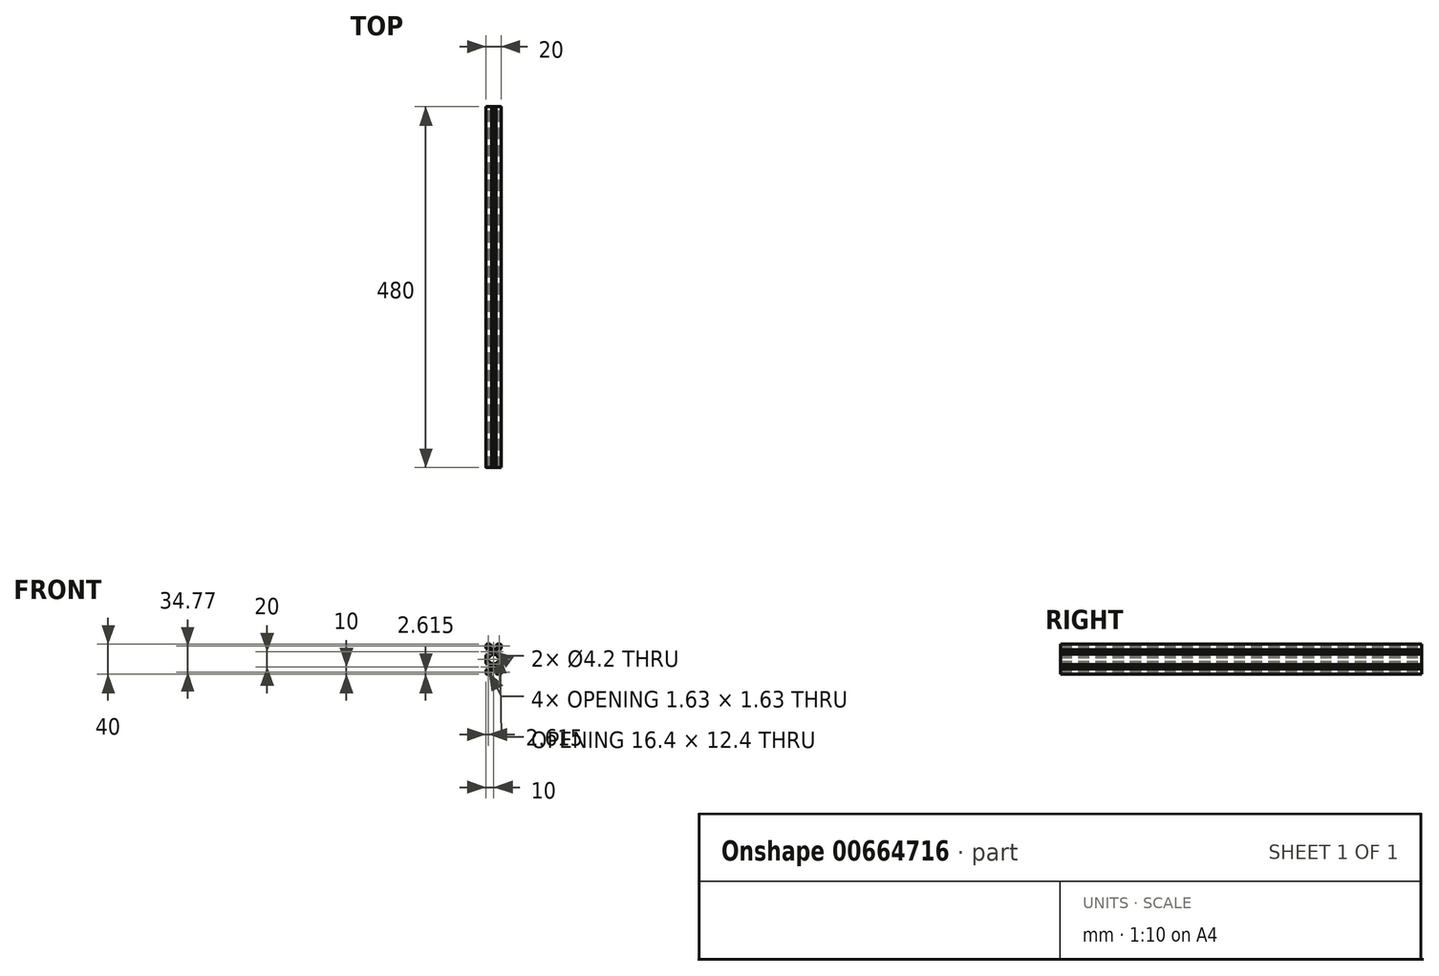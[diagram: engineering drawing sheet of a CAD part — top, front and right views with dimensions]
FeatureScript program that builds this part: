
annotation { "Feature Type Name" : "Feature", "Feature Type Description" : "" }
export const myFeature = defineFeature(function(context is Context, id is Id, definition is map)
    precondition{}
    {
        {
            var Q0;
            Q0=qCreatedBy(makeId("Front.planeOp"),FACE);
            var sketch = newSketch(context, id + "F0", { "sketchPlane" : qUnion([Q0])});
            skLineSegment(sketch, "E0", {"start": v(1.5, 0) * mm, "end": v(5.1, 0) * mm});
            skLineSegment(sketch, "E1", {"start": v(0, -1.5) * mm, "end": v(0, -5.1) * mm});
            skLineSegment(sketch, "E2", {"start": v(5.65, -0.23) * mm, "end": v(7.11, -1.69) * mm});
            skLineSegment(sketch, "E3", {"start": v(7.11, -1.7) * mm, "end": v(7.11, -1.8) * mm});
            skLineSegment(sketch, "E4", {"start": v(0.23, -5.65) * mm, "end": v(1.69, -7.11) * mm});
            skLineSegment(sketch, "E5", {"start": v(1.7, -7.11) * mm, "end": v(1.8, -7.11) * mm});
            skLineSegment(sketch, "E6", {"start": v(1.8, -7.11) * mm, "end": v(1.8, -4.5) * mm});
            skLineSegment(sketch, "E7", {"start": v(1.8, -4.5) * mm, "end": v(3.44, -4.5) * mm});
            skLineSegment(sketch, "E8", {"start": v(7.11, -1.8) * mm, "end": v(4.5, -1.8) * mm});
            skLineSegment(sketch, "E9", {"start": v(4.5, -1.8) * mm, "end": v(4.5, -3.44) * mm});
            skPoint(sketch, "E10.visualSharp", {"position": v(0, 0) * mm});
            skArc(sketch, "E10.filletArc", {"start": v(1.5, 0) * mm, "mid": v(0.44, -0.44) * mm, "end": v(0, -1.5) * mm});
            skPoint(sketch, "E11.visualSharp", {"position": v(5.42, 0) * mm});
            skArc(sketch, "E11.filletArc", {"start": v(5.65, -0.23) * mm, "mid": v(5.4, -0.06) * mm, "end": v(5.1, 0) * mm});
            skPoint(sketch, "E12.visualSharp", {"position": v(0, -5.42) * mm});
            skArc(sketch, "E12.filletArc", {"start": v(0, -5.1) * mm, "mid": v(0.06, -5.4) * mm, "end": v(0.23, -5.65) * mm});
            skLineSegment(sketch, "E13", {"start": v(1.8, -4.5) * mm, "end": v(1.8, 0) * mm, "construction": true});
            skLineSegment(sketch, "E14", {"start": v(4.5, -1.8) * mm, "end": v(0, -1.8) * mm, "construction": true});
            skPoint(sketch, "E15", {"position": v(1.8, -1.8) * mm});
            skLineSegment(sketch, "E16", {"start": v(1.8, -1.8) * mm, "end": v(3.43, -1.8) * mm});
            skLineSegment(sketch, "E17", {"start": v(3.43, -1.8) * mm, "end": v(3.43, -2.34) * mm});
            skLineSegment(sketch, "E18", {"start": v(1.8, -1.8) * mm, "end": v(1.8, -3.43) * mm});
            skLineSegment(sketch, "E19", {"start": v(1.8, -3.43) * mm, "end": v(2.34, -3.43) * mm});
            skLineSegment(sketch, "E20", {"start": v(2.34, -3.43) * mm, "end": v(3.43, -2.34) * mm});
            skArc(sketch, "E21", {"start": v(10, -7.9) * mm, "mid": v(8.52, -8.52) * mm, "end": v(7.9, -10) * mm});
            skLineSegment(sketch, "E22", {"start": v(10, -7.9) * mm, "end": v(10, -6.2) * mm, "construction": true});
            skLineSegment(sketch, "E23", {"start": v(9.9, -6.1) * mm, "end": v(7.16, -6.1) * mm});
            skLineSegment(sketch, "E24", {"start": v(7.16, -6.1) * mm, "end": v(4.5, -3.44) * mm});
            skLineSegment(sketch, "E25", {"start": v(7.9, -10) * mm, "end": v(6.2, -10) * mm, "construction": true});
            skLineSegment(sketch, "E26", {"start": v(6.1, -9.9) * mm, "end": v(6.1, -7.16) * mm});
            skLineSegment(sketch, "E27", {"start": v(6.1, -7.16) * mm, "end": v(3.44, -4.5) * mm});
            skLineSegment(sketch, "E28", {"start": v(1.8, -1.8) * mm, "end": v(10, -10) * mm, "construction": true});
            skLineSegment(sketch, "E29", {"start": v(6.2, -10) * mm, "end": v(6.1, -9.9) * mm});
            skLineSegment(sketch, "E30", {"start": v(10, -6.2) * mm, "end": v(9.9, -6.1) * mm});
            skArc(sketch, "E31", {"start": v(7.9, -10) * mm, "mid": v(8.52, -11.48) * mm, "end": v(10, -12.1) * mm});
            skLineSegment(sketch, "E32", {"start": v(6.2, -10) * mm, "end": v(6.1, -10.1) * mm});
            skLineSegment(sketch, "E33", {"start": v(6.1, -10.1) * mm, "end": v(6.1, -12.84) * mm});
            skLineSegment(sketch, "E34", {"start": v(10, -12.1) * mm, "end": v(10, -13.8) * mm, "construction": true});
            skLineSegment(sketch, "E35", {"start": v(10, -13.8) * mm, "end": v(9.9, -13.9) * mm});
            skLineSegment(sketch, "E36", {"start": v(9.9, -13.9) * mm, "end": v(7.16, -13.9) * mm});
            skLineSegment(sketch, "E37", {"start": v(6.1, -12.84) * mm, "end": v(7.16, -13.9) * mm, "construction": true});
            skLineSegment(sketch, "E38", {"start": v(7.16, -6.1) * mm, "end": v(6.1, -7.16) * mm, "construction": true});
            skLineSegment(sketch, "E39", {"start": v(6.1, -12.84) * mm, "end": v(3.44, -15.5) * mm});
            skLineSegment(sketch, "E40", {"start": v(7.16, -13.9) * mm, "end": v(3.76, -17.3) * mm});
            skLineSegment(sketch, "E41", {"start": v(10, -10) * mm, "end": v(1.8, -18.2) * mm, "construction": true});
            skLineSegment(sketch, "E42", {"start": v(3.44, -15.5) * mm, "end": v(1.8, -15.5) * mm});
            skLineSegment(sketch, "E43", {"start": v(1.8, -15.5) * mm, "end": v(1.8, -12.89) * mm});
            skLineSegment(sketch, "E44", {"start": v(1.8, -12.89) * mm, "end": v(1.7, -12.89) * mm});
            skLineSegment(sketch, "E45", {"start": v(1.7, -12.89) * mm, "end": v(0.23, -14.35) * mm});
            skLineSegment(sketch, "E46", {"start": v(0, -14.9) * mm, "end": v(0, -20) * mm});
            skLineSegment(sketch, "E47", {"start": v(0, -20) * mm, "end": v(1.8, -20) * mm, "construction": true});
            skLineSegment(sketch, "E48", {"start": v(1.8, -20) * mm, "end": v(1.8, -17.3) * mm});
            skLineSegment(sketch, "E49", {"start": v(1.8, -17.3) * mm, "end": v(3.76, -17.3) * mm});
            skPoint(sketch, "E50.visualSharp", {"position": v(0, -14.58) * mm});
            skArc(sketch, "E50.filletArc", {"start": v(0.23, -14.35) * mm, "mid": v(0.06, -14.6) * mm, "end": v(0, -14.9) * mm});
            skLineSegment(sketch, "E51.MirrorCS", {"start": v(13.8, -10) * mm, "end": v(13.9, -10.1) * mm});
            skLineSegment(sketch, "E52.MirrorCS", {"start": v(13.8, -10) * mm, "end": v(13.9, -9.9) * mm});
            skLineSegment(sketch, "E53.MirrorCS", {"start": v(12.9, -1.69) * mm, "end": v(12.9, -1.8) * mm});
            skLineSegment(sketch, "E54.MirrorCS", {"start": v(16.57, -1.8) * mm, "end": v(16.57, -2.34) * mm});
            skLineSegment(sketch, "E55.MirrorCS", {"start": v(10, -13.8) * mm, "end": v(10.1, -13.9) * mm});
            skLineSegment(sketch, "E56.MirrorCS", {"start": v(12.84, -6.1) * mm, "end": v(13.9, -7.16) * mm, "construction": true});
            skArc(sketch, "E57.MirrorCS", {"start": v(14.35, -0.23) * mm, "mid": v(14.6, -0.06) * mm, "end": v(14.9, 0) * mm});
            skArc(sketch, "E58.MirrorCS", {"start": v(20, -5.1) * mm, "mid": v(19.94, -5.4) * mm, "end": v(19.77, -5.65) * mm});
            skLineSegment(sketch, "E59.MirrorCS", {"start": v(13.9, -12.84) * mm, "end": v(12.84, -13.9) * mm, "construction": true});
            skArc(sketch, "E60.MirrorCS", {"start": v(19.77, -14.35) * mm, "mid": v(19.94, -14.6) * mm, "end": v(20, -14.9) * mm});
            skLineSegment(sketch, "E61.MirrorCS", {"start": v(18.31, -7.11) * mm, "end": v(18.2, -7.11) * mm});
            skLineSegment(sketch, "E62.MirrorCS", {"start": v(10, -6.2) * mm, "end": v(10.1, -6.1) * mm});
            skLineSegment(sketch, "E63.MirrorCS", {"start": v(18.2, -3.43) * mm, "end": v(17.66, -3.43) * mm});
            skLineSegment(sketch, "E64.MirrorCS", {"start": v(18.2, -12.89) * mm, "end": v(18.31, -12.89) * mm});
            skLineSegment(sketch, "E65.MirrorCS", {"start": v(17.66, -3.43) * mm, "end": v(16.57, -2.34) * mm});
            skLineSegment(sketch, "E66.MirrorCS", {"start": v(18.31, -12.89) * mm, "end": v(19.77, -14.35) * mm});
            skLineSegment(sketch, "E67.MirrorCS", {"start": v(18.2, -1.8) * mm, "end": v(16.57, -1.8) * mm});
            skArc(sketch, "E68.MirrorCS", {"start": v(18.5, 0) * mm, "mid": v(19.56, -0.44) * mm, "end": v(20, -1.5) * mm});
            skLineSegment(sketch, "E69.MirrorCS", {"start": v(15.5, -1.8) * mm, "end": v(15.5, -3.44) * mm});
            skLineSegment(sketch, "E70.MirrorCS", {"start": v(12.1, -10) * mm, "end": v(13.8, -10) * mm, "construction": true});
            skLineSegment(sketch, "E71.MirrorCS", {"start": v(18.2, -1.8) * mm, "end": v(18.2, -3.43) * mm});
            skPoint(sketch, "E72.MirrorP", {"position": v(18.2, -1.8) * mm});
            skLineSegment(sketch, "E73.MirrorCS", {"start": v(10.1, -6.1) * mm, "end": v(12.84, -6.1) * mm});
            skLineSegment(sketch, "E74.MirrorCS", {"start": v(20, -20) * mm, "end": v(18.2, -20) * mm, "construction": true});
            skLineSegment(sketch, "E75.MirrorCS", {"start": v(18.2, -7.11) * mm, "end": v(18.2, -4.5) * mm});
            skLineSegment(sketch, "E76.MirrorCS", {"start": v(18.5, 0) * mm, "end": v(14.9, 0) * mm});
            skLineSegment(sketch, "E77.MirrorCS", {"start": v(12.84, -6.1) * mm, "end": v(15.5, -3.44) * mm});
            skArc(sketch, "E78.MirrorCS", {"start": v(12.1, -10) * mm, "mid": v(11.48, -11.48) * mm, "end": v(10, -12.1) * mm});
            skLineSegment(sketch, "E79.MirrorCS", {"start": v(12.84, -13.9) * mm, "end": v(16.24, -17.3) * mm});
            skLineSegment(sketch, "E80.MirrorCS", {"start": v(13.9, -7.16) * mm, "end": v(16.56, -4.5) * mm});
            skLineSegment(sketch, "E81.MirrorCS", {"start": v(20, -14.9) * mm, "end": v(20, -20) * mm});
            skLineSegment(sketch, "E82.MirrorCS", {"start": v(13.9, -12.84) * mm, "end": v(16.56, -15.5) * mm});
            skLineSegment(sketch, "E83.MirrorCS", {"start": v(18.2, -20) * mm, "end": v(18.2, -17.3) * mm});
            skLineSegment(sketch, "E84.MirrorCS", {"start": v(14.35, -0.23) * mm, "end": v(12.9, -1.69) * mm});
            skPoint(sketch, "E85.MirrorP", {"position": v(20, 0) * mm});
            skLineSegment(sketch, "E86.MirrorCS", {"start": v(18.2, -4.5) * mm, "end": v(16.56, -4.5) * mm});
            skLineSegment(sketch, "E87.MirrorCS", {"start": v(12.9, -1.8) * mm, "end": v(15.5, -1.8) * mm});
            skPoint(sketch, "E88.MirrorP", {"position": v(20, -14.58) * mm});
            skLineSegment(sketch, "E89.MirrorCS", {"start": v(20, -1.5) * mm, "end": v(20, -5.1) * mm});
            skLineSegment(sketch, "E90.MirrorCS", {"start": v(18.2, -15.5) * mm, "end": v(18.2, -12.89) * mm});
            skLineSegment(sketch, "E91.MirrorCS", {"start": v(16.56, -15.5) * mm, "end": v(18.2, -15.5) * mm});
            skLineSegment(sketch, "E92.MirrorCS", {"start": v(13.9, -9.9) * mm, "end": v(13.9, -7.16) * mm});
            skArc(sketch, "E93.MirrorCS", {"start": v(10, -7.9) * mm, "mid": v(11.48, -8.52) * mm, "end": v(12.1, -10) * mm});
            skPoint(sketch, "E94.MirrorP", {"position": v(14.58, 0) * mm});
            skLineSegment(sketch, "E95.MirrorCS", {"start": v(18.2, -4.5) * mm, "end": v(18.2, 0) * mm, "construction": true});
            skLineSegment(sketch, "E96.MirrorCS", {"start": v(15.5, -1.8) * mm, "end": v(20, -1.8) * mm, "construction": true});
            skLineSegment(sketch, "E97.MirrorCS", {"start": v(10, -10) * mm, "end": v(18.2, -18.2) * mm, "construction": true});
            skLineSegment(sketch, "E98.MirrorCS", {"start": v(18.2, -17.3) * mm, "end": v(16.24, -17.3) * mm});
            skLineSegment(sketch, "E99.MirrorCS", {"start": v(18.2, -1.8) * mm, "end": v(10, -10) * mm, "construction": true});
            skLineSegment(sketch, "E100.MirrorCS", {"start": v(10.1, -13.9) * mm, "end": v(12.84, -13.9) * mm});
            skPoint(sketch, "E101.MirrorP", {"position": v(20, -5.42) * mm});
            skLineSegment(sketch, "E102.MirrorCS", {"start": v(19.77, -5.65) * mm, "end": v(18.31, -7.11) * mm});
            skLineSegment(sketch, "E103.MirrorCS", {"start": v(13.9, -10.1) * mm, "end": v(13.9, -12.84) * mm});
            skLineSegment(sketch, "E104.MirrorCS", {"start": v(6.2, -30) * mm, "end": v(6.1, -29.9) * mm});
            skLineSegment(sketch, "E105.MirrorCS", {"start": v(6.2, -30) * mm, "end": v(6.1, -30.1) * mm});
            skLineSegment(sketch, "E106.MirrorCS", {"start": v(13.8, -30) * mm, "end": v(13.9, -30.1) * mm});
            skLineSegment(sketch, "E107.MirrorCS", {"start": v(13.8, -30) * mm, "end": v(13.9, -29.9) * mm});
            skLineSegment(sketch, "E108.MirrorCS", {"start": v(10, -26.2) * mm, "end": v(9.9, -26.1) * mm});
            skLineSegment(sketch, "E109.MirrorCS", {"start": v(10, -26.2) * mm, "end": v(10.1, -26.1) * mm});
            skArc(sketch, "E110.MirrorCS", {"start": v(14.35, -39.77) * mm, "mid": v(14.6, -39.94) * mm, "end": v(14.9, -40) * mm});
            skLineSegment(sketch, "E111.MirrorCS", {"start": v(10, -33.8) * mm, "end": v(9.9, -33.9) * mm});
            skArc(sketch, "E112.MirrorCS", {"start": v(0.23, -25.65) * mm, "mid": v(0.06, -25.4) * mm, "end": v(0, -25.1) * mm});
            skArc(sketch, "E113.MirrorCS", {"start": v(19.77, -25.65) * mm, "mid": v(19.94, -25.4) * mm, "end": v(20, -25.1) * mm});
            skArc(sketch, "E114.MirrorCS", {"start": v(5.65, -39.77) * mm, "mid": v(5.4, -39.94) * mm, "end": v(5.1, -40) * mm});
            skLineSegment(sketch, "E115.MirrorCS", {"start": v(10, -33.8) * mm, "end": v(10.1, -33.9) * mm});
            skLineSegment(sketch, "E116.MirrorCS", {"start": v(7.11, -38.3) * mm, "end": v(7.11, -38.2) * mm});
            skLineSegment(sketch, "E117.MirrorCS", {"start": v(18.2, -36.57) * mm, "end": v(17.66, -36.57) * mm});
            skArc(sketch, "E118.MirrorCS", {"start": v(0, -34.9) * mm, "mid": v(0.06, -34.6) * mm, "end": v(0.23, -34.35) * mm});
            skLineSegment(sketch, "E119.MirrorCS", {"start": v(1.8, -36.57) * mm, "end": v(2.34, -36.57) * mm});
            skLineSegment(sketch, "E120.MirrorCS", {"start": v(3.43, -38.2) * mm, "end": v(3.43, -37.66) * mm});
            skLineSegment(sketch, "E121.MirrorCS", {"start": v(1.8, -27.11) * mm, "end": v(1.7, -27.11) * mm});
            skLineSegment(sketch, "E122.MirrorCS", {"start": v(18.31, -32.89) * mm, "end": v(18.2, -32.89) * mm});
            skLineSegment(sketch, "E123.MirrorCS", {"start": v(12.9, -38.31) * mm, "end": v(12.9, -38.2) * mm});
            skLineSegment(sketch, "E124.MirrorCS", {"start": v(16.57, -38.2) * mm, "end": v(16.57, -37.66) * mm});
            skLineSegment(sketch, "E125.MirrorCS", {"start": v(10, -27.9) * mm, "end": v(10, -26.2) * mm, "construction": true});
            skLineSegment(sketch, "E126.MirrorCS", {"start": v(1.7, -32.9) * mm, "end": v(1.8, -32.9) * mm});
            skLineSegment(sketch, "E127.MirrorCS", {"start": v(18.2, -27.11) * mm, "end": v(18.31, -27.11) * mm});
            skArc(sketch, "E128.MirrorCS", {"start": v(20, -34.9) * mm, "mid": v(19.94, -34.6) * mm, "end": v(19.77, -34.35) * mm});
            skLineSegment(sketch, "E129.MirrorCS", {"start": v(2.34, -36.57) * mm, "end": v(3.43, -37.66) * mm});
            skLineSegment(sketch, "E130.MirrorCS", {"start": v(13.9, -27.16) * mm, "end": v(12.84, -26.1) * mm, "construction": true});
            skLineSegment(sketch, "E131.MirrorCS", {"start": v(1.8, -38.2) * mm, "end": v(3.43, -38.2) * mm});
            skLineSegment(sketch, "E132.MirrorCS", {"start": v(1.69, -27.11) * mm, "end": v(0.23, -25.65) * mm});
            skLineSegment(sketch, "E133.MirrorCS", {"start": v(17.66, -36.57) * mm, "end": v(16.57, -37.66) * mm});
            skLineSegment(sketch, "E134.MirrorCS", {"start": v(4.5, -38.2) * mm, "end": v(4.5, -36.56) * mm});
            skLineSegment(sketch, "E135.MirrorCS", {"start": v(6.1, -27.16) * mm, "end": v(7.16, -26.1) * mm, "construction": true});
            skLineSegment(sketch, "E136.MirrorCS", {"start": v(1.8, -38.2) * mm, "end": v(1.8, -36.57) * mm});
            skLineSegment(sketch, "E137.MirrorCS", {"start": v(18.2, -38.2) * mm, "end": v(18.2, -36.57) * mm});
            skLineSegment(sketch, "E138.MirrorCS", {"start": v(18.2, -38.2) * mm, "end": v(16.57, -38.2) * mm});
            skPoint(sketch, "E139.MirrorP", {"position": v(20, -40) * mm});
            skLineSegment(sketch, "E140.MirrorCS", {"start": v(18.2, -22.7) * mm, "end": v(16.24, -22.7) * mm});
            skLineSegment(sketch, "E141.MirrorCS", {"start": v(7.16, -26.1) * mm, "end": v(3.76, -22.7) * mm});
            skPoint(sketch, "E142.MirrorP", {"position": v(18.2, -38.2) * mm});
            skPoint(sketch, "E143.MirrorP", {"position": v(14.58, -40) * mm});
            skLineSegment(sketch, "E144.MirrorCS", {"start": v(6.1, -32.84) * mm, "end": v(3.44, -35.5) * mm});
            skArc(sketch, "E145.MirrorCS", {"start": v(18.5, -40) * mm, "mid": v(19.56, -39.56) * mm, "end": v(20, -38.5) * mm});
            skLineSegment(sketch, "E146.MirrorCS", {"start": v(16.56, -24.5) * mm, "end": v(18.2, -24.5) * mm});
            skLineSegment(sketch, "E147.MirrorCS", {"start": v(19.77, -34.35) * mm, "end": v(18.31, -32.89) * mm});
            skLineSegment(sketch, "E148.MirrorCS", {"start": v(18.5, -40) * mm, "end": v(14.9, -40) * mm});
            skArc(sketch, "E149.MirrorCS", {"start": v(12.1, -30) * mm, "mid": v(11.48, -28.52) * mm, "end": v(10, -27.9) * mm});
            skLineSegment(sketch, "E150.MirrorCS", {"start": v(7.16, -33.9) * mm, "end": v(4.5, -36.56) * mm});
            skLineSegment(sketch, "E151.MirrorCS", {"start": v(12.1, -30) * mm, "end": v(13.8, -30) * mm, "construction": true});
            skLineSegment(sketch, "E152.MirrorCS", {"start": v(1.8, -35.5) * mm, "end": v(1.8, -40) * mm, "construction": true});
            skLineSegment(sketch, "E153.MirrorCS", {"start": v(18.2, -38.2) * mm, "end": v(10, -30) * mm, "construction": true});
            skLineSegment(sketch, "E154.MirrorCS", {"start": v(4.5, -38.2) * mm, "end": v(0, -38.2) * mm, "construction": true});
            skLineSegment(sketch, "E155.MirrorCS", {"start": v(10, -30) * mm, "end": v(18.2, -21.8) * mm, "construction": true});
            skLineSegment(sketch, "E156.MirrorCS", {"start": v(15.5, -38.2) * mm, "end": v(15.5, -36.56) * mm});
            skLineSegment(sketch, "E157.MirrorCS", {"start": v(1.5, -40) * mm, "end": v(5.1, -40) * mm});
            skLineSegment(sketch, "E158.MirrorCS", {"start": v(10, -32.1) * mm, "end": v(10, -33.8) * mm, "construction": true});
            skPoint(sketch, "E159.MirrorP", {"position": v(1.8, -38.2) * mm});
            skLineSegment(sketch, "E160.MirrorCS", {"start": v(7.9, -30) * mm, "end": v(6.2, -30) * mm, "construction": true});
            skArc(sketch, "E161.MirrorCS", {"start": v(1.5, -40) * mm, "mid": v(0.44, -39.56) * mm, "end": v(0, -38.5) * mm});
            skLineSegment(sketch, "E162.MirrorCS", {"start": v(12.84, -26.1) * mm, "end": v(16.24, -22.7) * mm});
            skLineSegment(sketch, "E163.MirrorCS", {"start": v(12.9, -38.2) * mm, "end": v(15.5, -38.2) * mm});
            skLineSegment(sketch, "E164.MirrorCS", {"start": v(7.11, -38.2) * mm, "end": v(4.5, -38.2) * mm});
            skLineSegment(sketch, "E165.MirrorCS", {"start": v(1.8, -35.5) * mm, "end": v(3.44, -35.5) * mm});
            skLineSegment(sketch, "E166.MirrorCS", {"start": v(7.16, -33.9) * mm, "end": v(6.1, -32.84) * mm, "construction": true});
            skLineSegment(sketch, "E167.MirrorCS", {"start": v(10.1, -33.9) * mm, "end": v(12.84, -33.9) * mm});
            skLineSegment(sketch, "E168.MirrorCS", {"start": v(13.9, -27.16) * mm, "end": v(16.56, -24.5) * mm});
            skLineSegment(sketch, "E169.MirrorCS", {"start": v(1.8, -38.2) * mm, "end": v(10, -30) * mm, "construction": true});
            skLineSegment(sketch, "E170.MirrorCS", {"start": v(12.84, -33.9) * mm, "end": v(15.5, -36.56) * mm});
            skLineSegment(sketch, "E171.MirrorCS", {"start": v(15.5, -38.2) * mm, "end": v(20, -38.2) * mm, "construction": true});
            skPoint(sketch, "E172.MirrorP", {"position": v(0, -25.42) * mm});
            skLineSegment(sketch, "E173.MirrorCS", {"start": v(18.2, -35.5) * mm, "end": v(18.2, -40) * mm, "construction": true});
            skLineSegment(sketch, "E174.MirrorCS", {"start": v(18.2, -35.5) * mm, "end": v(16.56, -35.5) * mm});
            skLineSegment(sketch, "E175.MirrorCS", {"start": v(18.2, -24.5) * mm, "end": v(18.2, -27.11) * mm});
            skLineSegment(sketch, "E176.MirrorCS", {"start": v(9.9, -33.9) * mm, "end": v(7.16, -33.9) * mm});
            skLineSegment(sketch, "E177.MirrorCS", {"start": v(13.9, -29.9) * mm, "end": v(13.9, -27.16) * mm});
            skLineSegment(sketch, "E178.MirrorCS", {"start": v(20, -38.5) * mm, "end": v(20, -34.9) * mm});
            skLineSegment(sketch, "E179.MirrorCS", {"start": v(13.9, -32.84) * mm, "end": v(16.56, -35.5) * mm});
            skLineSegment(sketch, "E180.MirrorCS", {"start": v(18.2, -20) * mm, "end": v(18.2, -22.7) * mm});
            skArc(sketch, "E181.MirrorCS", {"start": v(10, -32.1) * mm, "mid": v(8.52, -31.48) * mm, "end": v(7.9, -30) * mm});
            skLineSegment(sketch, "E182.MirrorCS", {"start": v(12.84, -33.9) * mm, "end": v(13.9, -32.84) * mm, "construction": true});
            skLineSegment(sketch, "E183.MirrorCS", {"start": v(5.65, -39.77) * mm, "end": v(7.11, -38.31) * mm});
            skLineSegment(sketch, "E184.MirrorCS", {"start": v(10, -30) * mm, "end": v(1.8, -21.8) * mm, "construction": true});
            skLineSegment(sketch, "E185.MirrorCS", {"start": v(20, -25.1) * mm, "end": v(20, -20) * mm});
            skLineSegment(sketch, "E186.MirrorCS", {"start": v(9.9, -26.1) * mm, "end": v(7.16, -26.1) * mm});
            skArc(sketch, "E187.MirrorCS", {"start": v(7.9, -30) * mm, "mid": v(8.52, -28.52) * mm, "end": v(10, -27.9) * mm});
            skLineSegment(sketch, "E188.MirrorCS", {"start": v(18.31, -27.11) * mm, "end": v(19.77, -25.65) * mm});
            skArc(sketch, "E189.MirrorCS", {"start": v(10, -32.1) * mm, "mid": v(11.48, -31.48) * mm, "end": v(12.1, -30) * mm});
            skLineSegment(sketch, "E190.MirrorCS", {"start": v(1.8, -32.9) * mm, "end": v(1.8, -35.5) * mm});
            skLineSegment(sketch, "E191.MirrorCS", {"start": v(1.8, -22.7) * mm, "end": v(3.76, -22.7) * mm});
            skLineSegment(sketch, "E192.MirrorCS", {"start": v(0, -25.1) * mm, "end": v(0, -20) * mm});
            skLineSegment(sketch, "E193.MirrorCS", {"start": v(1.8, -24.5) * mm, "end": v(1.8, -27.11) * mm});
            skLineSegment(sketch, "E194.MirrorCS", {"start": v(14.35, -39.77) * mm, "end": v(12.9, -38.31) * mm});
            skLineSegment(sketch, "E195.MirrorCS", {"start": v(10.1, -26.1) * mm, "end": v(12.84, -26.1) * mm});
            skPoint(sketch, "E196.MirrorP", {"position": v(20, -34.58) * mm});
            skPoint(sketch, "E197.MirrorP", {"position": v(0, -40) * mm});
            skPoint(sketch, "E198.MirrorP", {"position": v(20, -25.42) * mm});
            skLineSegment(sketch, "E199.MirrorCS", {"start": v(0.23, -34.35) * mm, "end": v(1.69, -32.89) * mm});
            skLineSegment(sketch, "E200.MirrorCS", {"start": v(0, -38.5) * mm, "end": v(0, -34.9) * mm});
            skLineSegment(sketch, "E201.MirrorCS", {"start": v(18.2, -32.89) * mm, "end": v(18.2, -35.5) * mm});
            skLineSegment(sketch, "E202.MirrorCS", {"start": v(1.8, -20) * mm, "end": v(1.8, -22.7) * mm});
            skLineSegment(sketch, "E203.MirrorCS", {"start": v(6.1, -29.9) * mm, "end": v(6.1, -27.16) * mm});
            skPoint(sketch, "E204.MirrorP", {"position": v(0, -34.58) * mm});
            skLineSegment(sketch, "E205.MirrorCS", {"start": v(6.1, -27.16) * mm, "end": v(3.44, -24.5) * mm});
            skLineSegment(sketch, "E206.MirrorCS", {"start": v(3.44, -24.5) * mm, "end": v(1.8, -24.5) * mm});
            skPoint(sketch, "E207.MirrorP", {"position": v(5.42, -40) * mm});
            skLineSegment(sketch, "E208.MirrorCS", {"start": v(6.1, -30.1) * mm, "end": v(6.1, -32.84) * mm});
            skLineSegment(sketch, "E209.MirrorCS", {"start": v(13.9, -30.1) * mm, "end": v(13.9, -32.84) * mm});
            skSolve(sketch);
        }
        {
            assignVariable(context, id + "F1", {"name" : "L", "anyValue" : 480 * mm});
        }
        {
            var Q0;
            Q0=qSketchRegion(id+"F0",true);
            extrude(context, id + "F2", {"entities" : qUnion([Q0]), "depth" : getVariable(context, 'L')});
        }
    });
